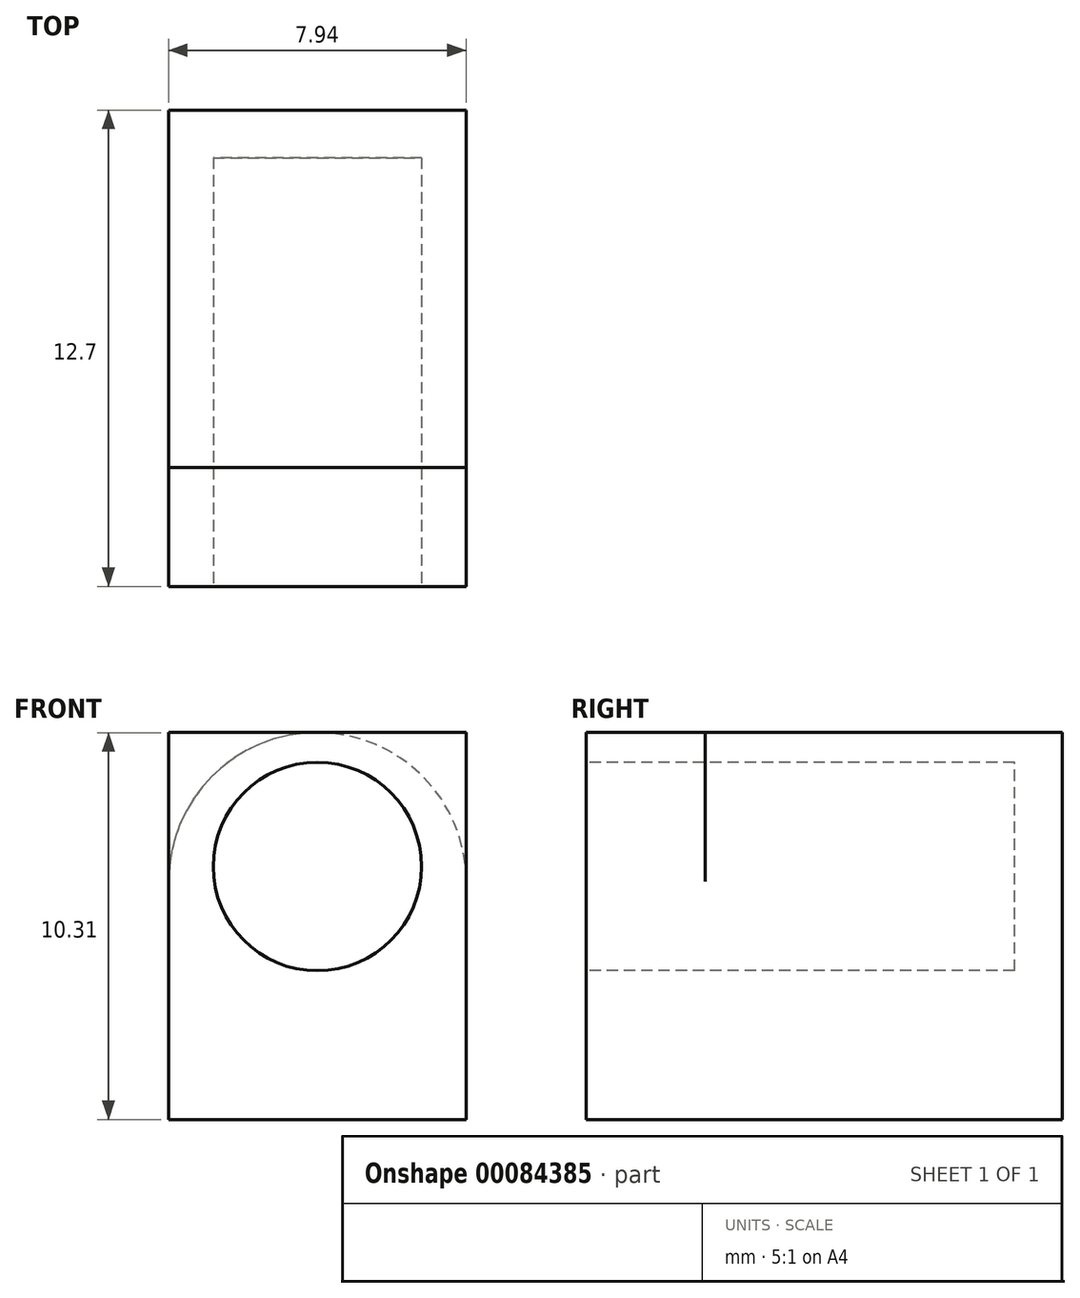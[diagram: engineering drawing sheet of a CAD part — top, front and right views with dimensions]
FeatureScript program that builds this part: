
annotation { "Feature Type Name" : "Feature", "Feature Type Description" : "" }
export const myFeature = defineFeature(function(context is Context, id is Id, definition is map)
    precondition{}
    {
        {
            var Q0;
            Q0=qCreatedBy(makeId("Front.planeOp"),FACE);
            var sketch = newSketch(context, id + "F0", { "sketchPlane" : qUnion([Q0])});
            skLineSegment(sketch, "E0", {"start": v(-19.97, 2.5) * mm, "end": v(-19.97, -7.81) * mm});
            skLineSegment(sketch, "E1", {"start": v(-19.97, 2.5) * mm, "end": v(-12.03, 2.5) * mm});
            skLineSegment(sketch, "E2", {"start": v(-12.03, 2.5) * mm, "end": v(-12.03, -7.81) * mm});
            skLineSegment(sketch, "E3", {"start": v(-19.97, -7.81) * mm, "end": v(-12.03, -7.81) * mm});
            skArc(sketch, "E4", {"start": v(-12.03, -1.46) * mm, "mid": v(-16, 2.5) * mm, "end": v(-19.97, -1.46) * mm});
            skLineSegment(sketch, "E5", {"start": v(-19.97, -1.46) * mm, "end": v(-12.03, -1.46) * mm});
            skSolve(sketch);
        }
        {
            var Q0;
            {var subQ0=sQuery(id+"F0.wireOp",EDGE,"E3");Q0=makeQuery(id+"F0.imprint","IMPRINT",FACE,{"disambiguationData":[TD([[makeQuery(id+"F0.imprint","IMPRINT",EDGE,{"derivedFrom":subQ0}),1.0]])]});}
            var Q1;
            {var subQ0=sQuery(id+"F0.wireOp",EDGE,"E5");Q1=makeQuery(id+"F0.imprint","IMPRINT",FACE,{"disambiguationData":[TD([[makeQuery(id+"F0.imprint","IMPRINT",EDGE,{"derivedFrom":subQ0}),1.0]])]});}
            extrude(context, id + "F1", {"entities" : qUnion([Q0, Q1]), "depth" : 9.52 * mm});
        }
        {
            var Q0;
            Q0=makeQuery(id+"F1.opExtrude","CAP_FACE",FACE,{"disambiguationData":[OSD([sQuery(id+"F0.wireOp",EDGE,"E0"),sQuery(id+"F0.wireOp",EDGE,"E1"),sQuery(id+"F0.wireOp",EDGE,"E2"),sQuery(id+"F0.wireOp",EDGE,"E3")])],"isStart":false});
            var sketch = newSketch(context, id + "F2", { "sketchPlane" : qUnion([Q0])});
            skSolve(sketch);
        }
        {
            var Q0;
            Q0=makeQuery(id+"F2.imprint","IMPRINT",FACE,{"disambiguationData":[TD([[makeQuery(id+"F2.imprint","IMPRINT",EDGE,{"derivedFrom":makeQuery(id+"F1.opExtrude","CAP_EDGE",EDGE,{"disambiguationData":[OSD([sQuery(id+"F0.wireOp",EDGE,"E0")])],"isStart":false})}),1.0]])]});
            var sketch = newSketch(context, id + "F3", { "sketchPlane" : qUnion([Q0])});
            skLineSegment(sketch, "E6.bottom", {"start": v(-12.03, -7.81) * mm, "end": v(-19.97, -7.81) * mm});
            skLineSegment(sketch, "E6.top", {"start": v(-12.03, 2.5) * mm, "end": v(-19.97, 2.5) * mm});
            skLineSegment(sketch, "E6.left", {"start": v(-12.03, -7.81) * mm, "end": v(-12.03, 2.5) * mm});
            skLineSegment(sketch, "E6.right", {"start": v(-19.97, -7.81) * mm, "end": v(-19.97, 2.5) * mm});
            skSolve(sketch);
        }
        {
            var Q0;
            Q0 = qSketchRegion(id + "F3", true);
            extrude(context, id + "F4", {"entities" : qUnion([Q0]), "operationType" : NewBodyOperationType.ADD, "depth" : 3.17 * mm});
        }
        {
            var Q0;
            Q0=makeQuery(id+"F4.opExtrude","CAP_FACE",FACE,{"disambiguationData":[OSD([sQuery(id+"F3.wireOp",EDGE,"E6.bottom"),sQuery(id+"F3.wireOp",EDGE,"E6.top"),sQuery(id+"F3.wireOp",EDGE,"E6.left"),sQuery(id+"F3.wireOp",EDGE,"E6.right")])],"isStart":false});
            var sketch = newSketch(context, id + "F5", { "sketchPlane" : qUnion([Q0])});
            skCircle(sketch, "E7", {"center": v(-16, -1.07) * mm, "radius": 2.78 * mm});
            skPoint(sketch, "E7.centerSnap0", {"position": v(-16, -7.81) * mm});
            skSolve(sketch);
        }
        {
            var Q0;
            Q0 = qSketchRegion(id + "F5", true);
            extrude(context, id + "F6", {"entities" : qUnion([Q0]), "operationType" : NewBodyOperationType.REMOVE, "oppositeDirection" : true, "depth" : 11.43 * mm});
        }
    });
